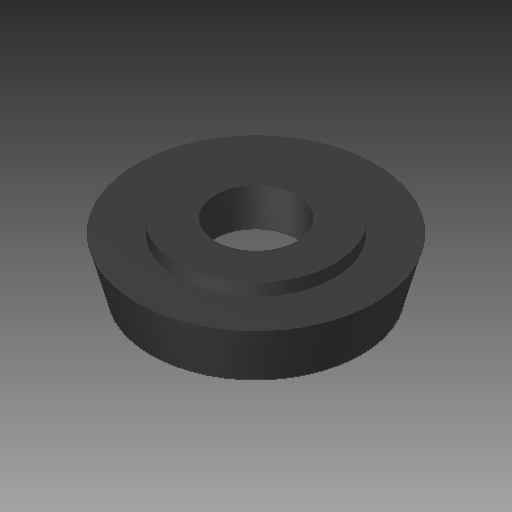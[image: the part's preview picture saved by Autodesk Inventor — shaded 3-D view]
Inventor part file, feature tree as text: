
AUTODESK INVENTOR PART (.ipt)
format: ipt  version: 2019.4 (Build 234330000, 330)  size: 109,056 bytes
history: mixed  units: mm
features: revolve x1, imported_body x1
ambient origin geometry x8: Origin, YZ Plane, XZ Plane, XY Plane, X Axis, Y Axis, Z Axis, Center Point
bodies: Solid1 (imported_parasolid)
feature tree (2):
  revolve  "Revolve1"  [1 undecoded]
  imported_body  NMx_Import_Brep_tag  [imported B-rep: ~8 faces, bbox_mm=[0.0, 2.5, 2.985898]]
note: 1 required parameter value undecoded (feature->parameter linkage not recoverable at this tier; creation-order binding heuristic only, values carry confidence <= 0.55)
